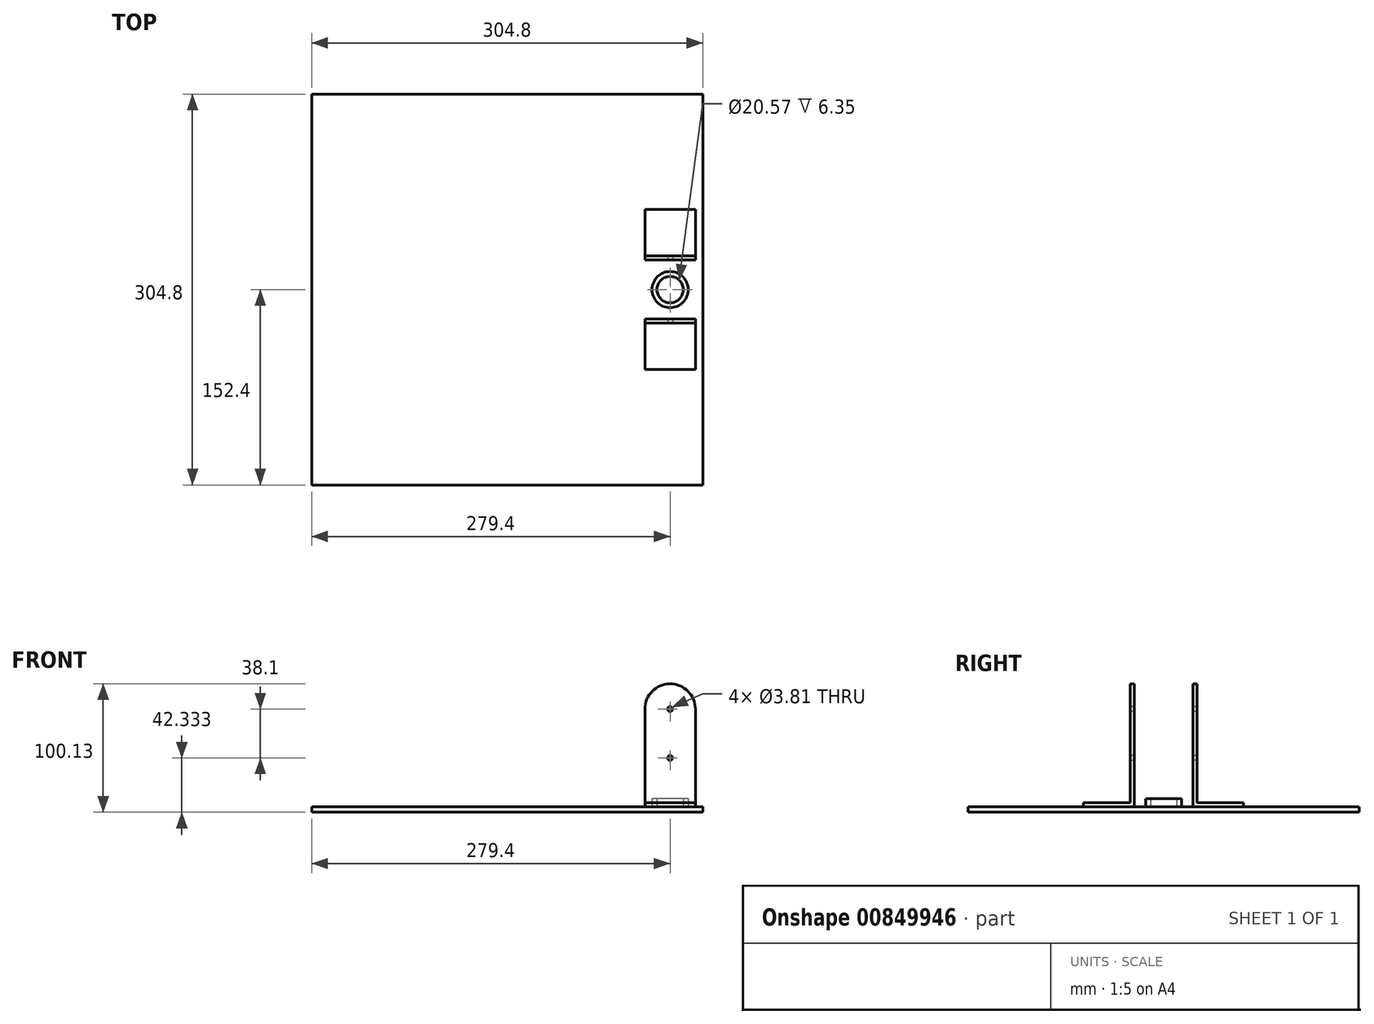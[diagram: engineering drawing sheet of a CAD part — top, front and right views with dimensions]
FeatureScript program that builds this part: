
annotation { "Feature Type Name" : "Feature", "Feature Type Description" : "" }
export const myFeature = defineFeature(function(context is Context, id is Id, definition is map)
    precondition{}
    {
        {
            var Q0;
            Q0=qCreatedBy(makeId("Top.planeOp"),FACE);
            var sketch = newSketch(context, id + "F0", { "sketchPlane" : qUnion([Q0])});
            skLineSegment(sketch, "E0.bottom", {"start": v(-152.4, 152.4) * mm, "end": v(152.4, 152.4) * mm});
            skLineSegment(sketch, "E0.top", {"start": v(-152.4, -152.4) * mm, "end": v(152.4, -152.4) * mm});
            skLineSegment(sketch, "E0.left", {"start": v(-152.4, 152.4) * mm, "end": v(-152.4, -152.4) * mm});
            skLineSegment(sketch, "E0.right", {"start": v(152.4, 152.4) * mm, "end": v(152.4, -152.4) * mm});
            skPoint(sketch, "E1", {"position": v(0, 152.4) * mm});
            skPoint(sketch, "E2", {"position": v(152.4, 0) * mm});
            skSolve(sketch);
        }
        {
            var Q0;
            Q0 = qSketchRegion(id + "F0", true);
            extrude(context, id + "F1", {"entities" : qUnion([Q0]), "depth" : 4.23 * mm, "offsetDistance" : 25.4 * mm});
        }
        {
            var Q0;
            Q0=makeQuery(id+"F1.opExtrude","CAP_FACE",FACE,{"disambiguationData":[OSD([sQuery(id+"F0.wireOp",EDGE,"E0.bottom"),sQuery(id+"F0.wireOp",EDGE,"E0.top"),sQuery(id+"F0.wireOp",EDGE,"E0.left"),sQuery(id+"F0.wireOp",EDGE,"E0.right")])],"isStart":false});
            var sketch = newSketch(context, id + "F2", { "sketchPlane" : qUnion([Q0])});
            skCircle(sketch, "E3", {"center": v(127, 0) * mm, "radius": 10.29 * mm});
            skCircle(sketch, "E4", {"center": v(127, 0) * mm, "radius": 14.1 * mm});
            skSolve(sketch);
        }
        {
            var Q0;
            Q0 = qSketchRegion(id + "F2", true);
            extrude(context, id + "F3", {"entities" : qUnion([Q0]), "operationType" : NewBodyOperationType.ADD, "depth" : 6.35 * mm, "offsetDistance" : 25.4 * mm});
        }
        {
            var Q0;
            {var subQ0=sQuery(id+"F0.wireOp",EDGE,"E0.left");var subQ1=sQuery(id+"F0.wireOp",EDGE,"E0.top");var subQ2=sQuery(id+"F0.wireOp",EDGE,"E0.right");var subQ3=sQuery(id+"F0.wireOp",EDGE,"E0.bottom");Q0=makeQuery(id+"F3.boolean.opBoolean","SPLIT",FACE,{"disambiguationData":[TD([makeQuery(id+"F1.opExtrude","SWEPT_FACE",FACE,{"disambiguationData":[OSD([subQ3])]})])],"derivedFrom":makeQuery(id+"F1.opExtrude","CAP_FACE",FACE,{"disambiguationData":[OSD([subQ3,subQ1,subQ0,subQ2])],"isStart":false})});}
            var sketch = newSketch(context, id + "F4", { "sketchPlane" : qUnion([Q0])});
            skLineSegment(sketch, "E5.bottom", {"start": v(107.3, 62.38) * mm, "end": v(146.7, 62.38) * mm});
            skLineSegment(sketch, "E5.top", {"start": v(107.3, 22.99) * mm, "end": v(146.7, 22.99) * mm});
            skLineSegment(sketch, "E5.left", {"start": v(107.3, 62.38) * mm, "end": v(107.3, 22.99) * mm});
            skLineSegment(sketch, "E5.right", {"start": v(146.7, 62.38) * mm, "end": v(146.7, 22.99) * mm});
            skLineSegment(sketch, "E6.bottom", {"start": v(107.3, -22.99) * mm, "end": v(146.7, -22.99) * mm});
            skLineSegment(sketch, "E6.top", {"start": v(107.3, -62.38) * mm, "end": v(146.7, -62.38) * mm});
            skLineSegment(sketch, "E6.left", {"start": v(107.3, -22.99) * mm, "end": v(107.3, -62.38) * mm});
            skLineSegment(sketch, "E6.right", {"start": v(146.7, -22.99) * mm, "end": v(146.7, -62.38) * mm});
            skPoint(sketch, "E7", {"position": v(127, 62.38) * mm});
            skPoint(sketch, "E8", {"position": v(127, -22.99) * mm});
            skPoint(sketch, "E9", {"position": v(146.7, 42.68) * mm});
            skPoint(sketch, "E10", {"position": v(146.7, -42.68) * mm});
            skSolve(sketch);
        }
        {
            var Q0;
            Q0 = qSketchRegion(id + "F4", true);
            extrude(context, id + "F5", {"entities" : qUnion([Q0]), "operationType" : NewBodyOperationType.ADD, "depth" : 3.17 * mm, "offsetDistance" : 25.4 * mm});
        }
        {
            var Q0;
            Q0=makeQuery(id+"F5.opExtrude","SWEPT_FACE",FACE,{"disambiguationData":[OSD([sQuery(id+"F4.wireOp",EDGE,"E5.top")])]});
            var sketch = newSketch(context, id + "F6", { "sketchPlane" : qUnion([Q0])});
            skLineSegment(sketch, "E11.bottom", {"start": v(107.3, 4.23) * mm, "end": v(146.7, 4.23) * mm});
            skLineSegment(sketch, "E11.top", {"start": v(107.3, 80.43) * mm, "end": v(146.7, 80.43) * mm});
            skLineSegment(sketch, "E11.left", {"start": v(107.3, 4.23) * mm, "end": v(107.3, 80.43) * mm});
            skLineSegment(sketch, "E11.right", {"start": v(146.7, 4.23) * mm, "end": v(146.7, 80.43) * mm});
            skArc(sketch, "E12", {"start": v(146.7, 80.43) * mm, "mid": v(127, 100.13) * mm, "end": v(107.3, 80.43) * mm});
            skSolve(sketch);
        }
        {
            var Q0;
            Q0 = qSketchRegion(id + "F6", true);
            extrude(context, id + "F7", {"entities" : qUnion([Q0]), "operationType" : NewBodyOperationType.ADD, "oppositeDirection" : true, "depth" : 3.17 * mm, "offsetDistance" : 25.4 * mm});
        }
        {
            var Q0;
            Q0=makeQuery(id+"F1.opExtrude","SWEPT_BODY",BODY,{"disambiguationData":[OSD([sQuery(id+"F0.wireOp",EDGE,"E0.bottom"),sQuery(id+"F0.wireOp",EDGE,"E0.top"),sQuery(id+"F0.wireOp",EDGE,"E0.left"),sQuery(id+"F0.wireOp",EDGE,"E0.right")])]});
            var Q1;
            Q1=qCreatedBy(makeId("Front.planeOp"),FACE);
            mirror(context, id + "F8", {"operationType" : NewBodyOperationType.ADD, "entities" : qUnion([Q0]), "mirrorPlane" : qUnion([Q1])});
        }
        {
            var Q0;
            Q0=makeQuery(id+"F7.boolean.opBoolean","MERGE",FACE,{"derivedFrom":[makeQuery(id+"F5.opExtrude","SWEPT_FACE",FACE,{"disambiguationData":[OSD([sQuery(id+"F4.wireOp",EDGE,"E5.top")])]}),makeQuery(id+"F7.opExtrude","CAP_FACE",FACE,{"disambiguationData":[OSD([sQuery(id+"F6.wireOp",EDGE,"E11.bottom"),sQuery(id+"F6.wireOp",EDGE,"E11.left"),sQuery(id+"F6.wireOp",EDGE,"E11.right"),sQuery(id+"F6.wireOp",EDGE,"E12")])],"isStart":true})]});
            var sketch = newSketch(context, id + "F9", { "sketchPlane" : qUnion([Q0])});
            skCircle(sketch, "E13", {"center": v(127, 42.33) * mm, "radius": 1.9 * mm});
            skPoint(sketch, "E13.centerSnap0", {"position": v(127, 4.23) * mm});
            skCircle(sketch, "E14.0.1.0", {"center": v(127, 80.43) * mm, "radius": 1.9 * mm});
            skLineSegment(sketch, "E14.direction1", {"start": v(127, 42.33) * mm, "end": v(152.4, 42.33) * mm, "construction": true});
            skLineSegment(sketch, "E14.direction2", {"start": v(127, 42.33) * mm, "end": v(127, 80.43) * mm, "construction": true});
            skSolve(sketch);
        }
        {
            var Q0;
            Q0 = qSketchRegion(id + "F9", true);
            extrude(context, id + "F10", {"entities" : qUnion([Q0]), "operationType" : NewBodyOperationType.REMOVE, "endBound" : BoundingType.THROUGH_ALL, "oppositeDirection" : true, "depth" : 25.4 * mm, "offsetDistance" : 25.4 * mm, "hasSecondDirection" : true, "secondDirectionOppositeDirection" : false, "secondDirectionDepth" : 86.36 * mm});
        }
    });
